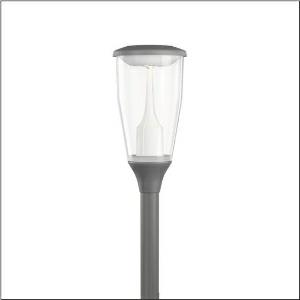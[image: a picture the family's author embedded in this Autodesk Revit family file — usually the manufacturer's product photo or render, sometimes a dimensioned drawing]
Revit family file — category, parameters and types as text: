
# Revit family: dl_11_iq___p1_0a_5xa5565nf14h000022_7674
name_source: partatom
category: Lighting Fixtures
units: mm (PartAtom-declared; Revit-internal decimal feet)

## family parameters
Cut with Voids When Loaded = No
Host = Face
Light Source = No
Part Type = Normal
Room Calculation Point = No
Round Connector Dimension = Use Diameter
Shared = No

## types (1)
- --- (1 x LED, 1530 lm, 11.8 W, 2700K)
    Apparent Load = 12 VA
    CIE Flux Codes = 34 63 91 95 100
    Color Rendering = 70
    Color Temperature = 2700K
    Default Elevation = 1800 mm
    Description = DL 11 iQ, mast luminaire, Module 540 iQ-SR, primary light control with 3 zone facetted reflector, of plastic, silver coated, highly specular, structured, primary optical cover: cover, of PMMA, transparent, light distribution: P1.0a, light emission: direct distribution, primary light characteristic: asymmetric, installation type: post-top, LED, High Power LED, rated luminous flux: 1.560lm, luminous efficacy: 149lm/W, light colour: 727, colour temperature: 2700K, control gear: iQ Street-Remote, control: Street-Remote, Auto-Match, Temp-Guard, Lumen-Switch, Night-Set, Smart-Wire, Light-Fading, Desk-Remote (wireless, voltage-free reading and setting of iQ features in the workshop via application-optimized NFC function/RFID function), optimised constant luminous flux control (CLO 2.0), mains connection: 220..240V, AC, 50/60Hz, connection cable pre-assembled, cable length: 5,5m, start of lifetime: 12W, end of service life: 12W, reduction: 5W, luminaire housing, upper part, of diecast aluminium, coated, SITECO metallic grey (DB 702S), spigot size: 60mm (post-top), mounting height: 3..5m, post-top mast mounting element, of diecast aluminium, coated, SITECO metallic grey (DB 702S), Module 540 iQ-SR, traffic white (RAL 9016), equipment: standard, protection rating (complete): IP66, insulation class (complete): insulation class II (safety insulation), certification: CE, ENEC, ENEC+, VDE, impact resistance: IK07, packaging unit: 1 piece

Light Distribution: P1.0a
    Height = 665 mm
    Lamp = 1 x LED
    Lamp Light Flux = 1530 lm
    Lamp Power = 11.8 W
    Lamp count = 1
    Length = 334 mm
    Luminous efficacy = 130 lm/W
    Manufacturer = Siteco
    ModVariant = No
    Model = 5XA5565NF14H000022
    Number of Poles = 1
    OnlyDefault = Yes
    Power Factor = 1
    Product Name = DL 11 iQ | P1.0a
    Product group = mast luminaire | pylon top
    ProductGroupID = 6100
    Protection Class = Protection class II
    Protection Degree = IP 66
    RLX_Detail_Level = 1
    RLX_Emergency_Light_Flux = 0 lm
    RLX_Emergency_Type = 0
    RLX_Emergency_Type_DB = No
    RlxData = <blob elided: 104273 chars, md5=5999eab7>
    Socket = socket
    Standby Power = 0 W
    System Light Flux = 1530 lm
    System Power = 12 W
    Type Comments = factory setting: luminous flux: 100 % | dim-lin: 254 | 472 mA
    Type Image = l_1258354.jpg
    URL = http://relux.com
    VarID = @adj_095681
    Voltage = 0 V
    Weight = 0.00 kg
    Width = 0 mm  [stored 0 ft]

note: [stored X ft] marks values corroborated as IEEE doubles in the binary element streams (Revit-internal decimal feet)

## geometry (parser evidence)
native form markers: Blend x4, Sweep x10
no freeform markers — native parametric forms only
